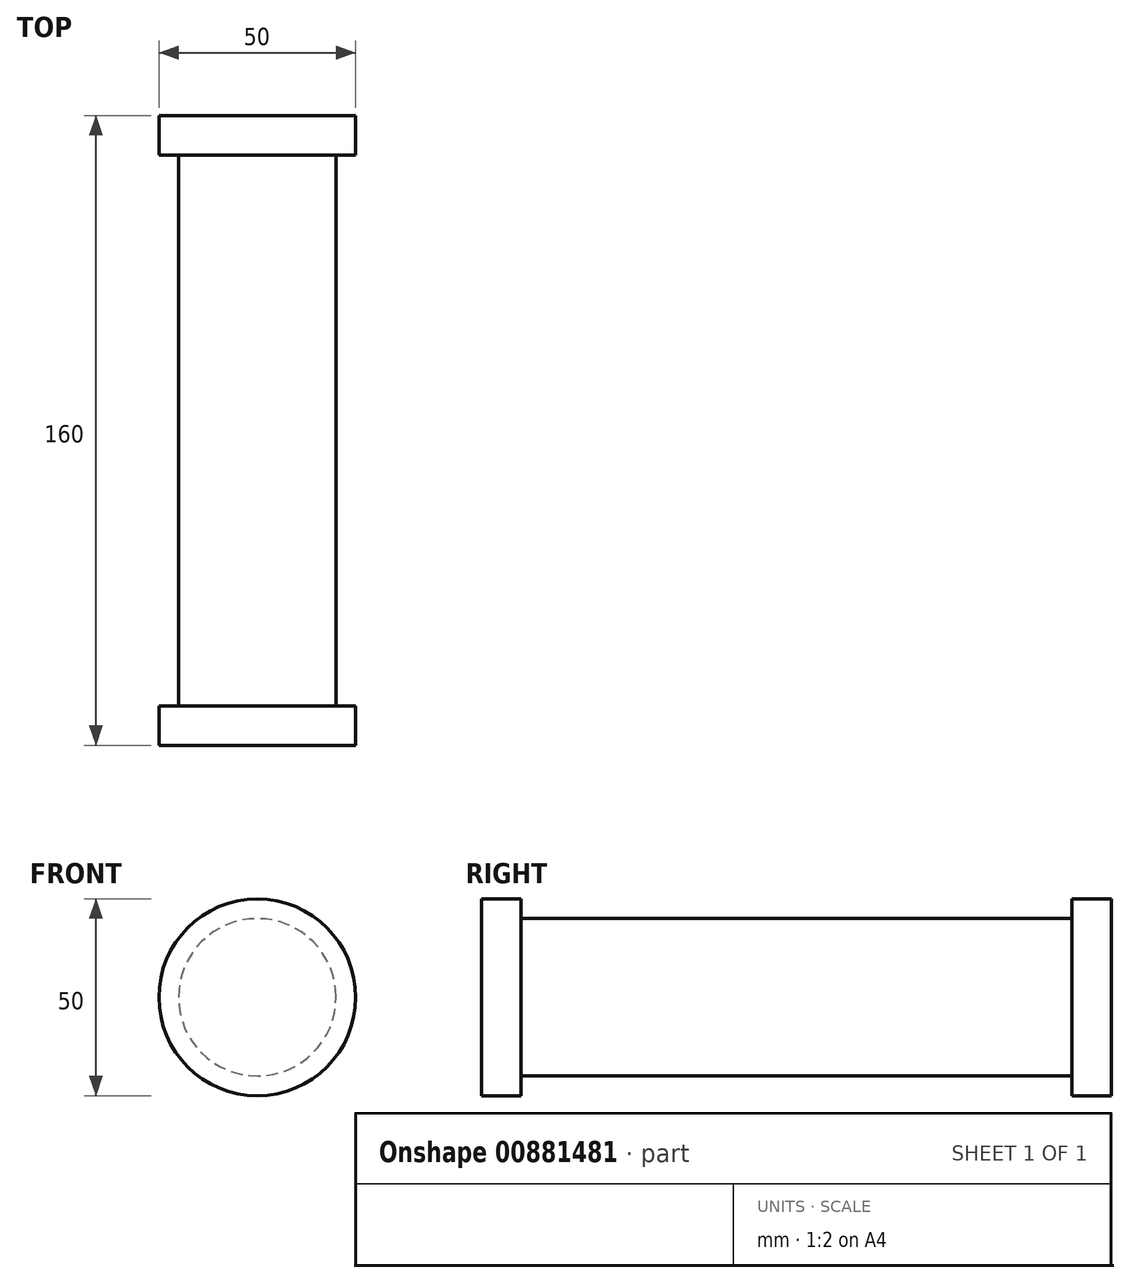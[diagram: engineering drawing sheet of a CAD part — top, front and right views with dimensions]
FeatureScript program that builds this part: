
annotation { "Feature Type Name" : "Feature", "Feature Type Description" : "" }
export const myFeature = defineFeature(function(context is Context, id is Id, definition is map)
    precondition{}
    {
        {
            var Q0;
            Q0=qCreatedBy(makeId("Front.planeOp"),FACE);
            var sketch = newSketch(context, id + "F0", { "sketchPlane" : qUnion([Q0])});
            skCircle(sketch, "E0.0", {"center": v(0, 0) * mm, "radius": 20 * mm});
            skCircle(sketch, "E1.0", {"center": v(0, 0) * mm, "radius": 25 * mm});
            skSolve(sketch);
        }
        {
            var Q0;
            Q0=makeQuery(id+"F0.imprint","IMPRINT",FACE,{"disambiguationData":[TD([[makeQuery(id+"F0.imprint","IMPRINT",EDGE,{"derivedFrom":sQuery(id+"F0.wireOp",EDGE,"E0.0")}),1.0]])]});
            extrude(context, id + "F1", {"entities" : qUnion([Q0]), "depth" : 140 * mm, "offsetDistance" : 25 * mm});
        }
        {
            var Q0;
            Q0=makeQuery(id+"F0.imprint","IMPRINT",FACE,{"disambiguationData":[TD([[makeQuery(id+"F0.imprint","IMPRINT",EDGE,{"derivedFrom":sQuery(id+"F0.wireOp",EDGE,"E0.0")}),-1.0]])]});
            var Q1;
            Q1=makeQuery(id+"F0.imprint","IMPRINT",FACE,{"disambiguationData":[TD([[makeQuery(id+"F0.imprint","IMPRINT",EDGE,{"derivedFrom":sQuery(id+"F0.wireOp",EDGE,"E0.0")}),1.0]])]});
            extrude(context, id + "F2", {"entities" : qUnion([Q0, Q1]), "operationType" : NewBodyOperationType.ADD, "oppositeDirection" : true, "depth" : 10 * mm, "offsetDistance" : 25 * mm});
        }
        {
            var Q0;
            Q0=makeQuery(id+"F1.opExtrude","CAP_FACE",FACE,{"disambiguationData":[OSD([sQuery(id+"F0.wireOp",EDGE,"E0.0")])],"isStart":false});
            var sketch = newSketch(context, id + "F3", { "sketchPlane" : qUnion([Q0])});
            skCircle(sketch, "E2.0", {"center": v(0, 0) * mm, "radius": 25 * mm});
            skSolve(sketch);
        }
        {
            var Q0;
            Q0 = qSketchRegion(id + "F3", true);
            extrude(context, id + "F4", {"entities" : qUnion([Q0]), "operationType" : NewBodyOperationType.ADD, "depth" : 10 * mm, "offsetDistance" : 25 * mm});
        }
    });
